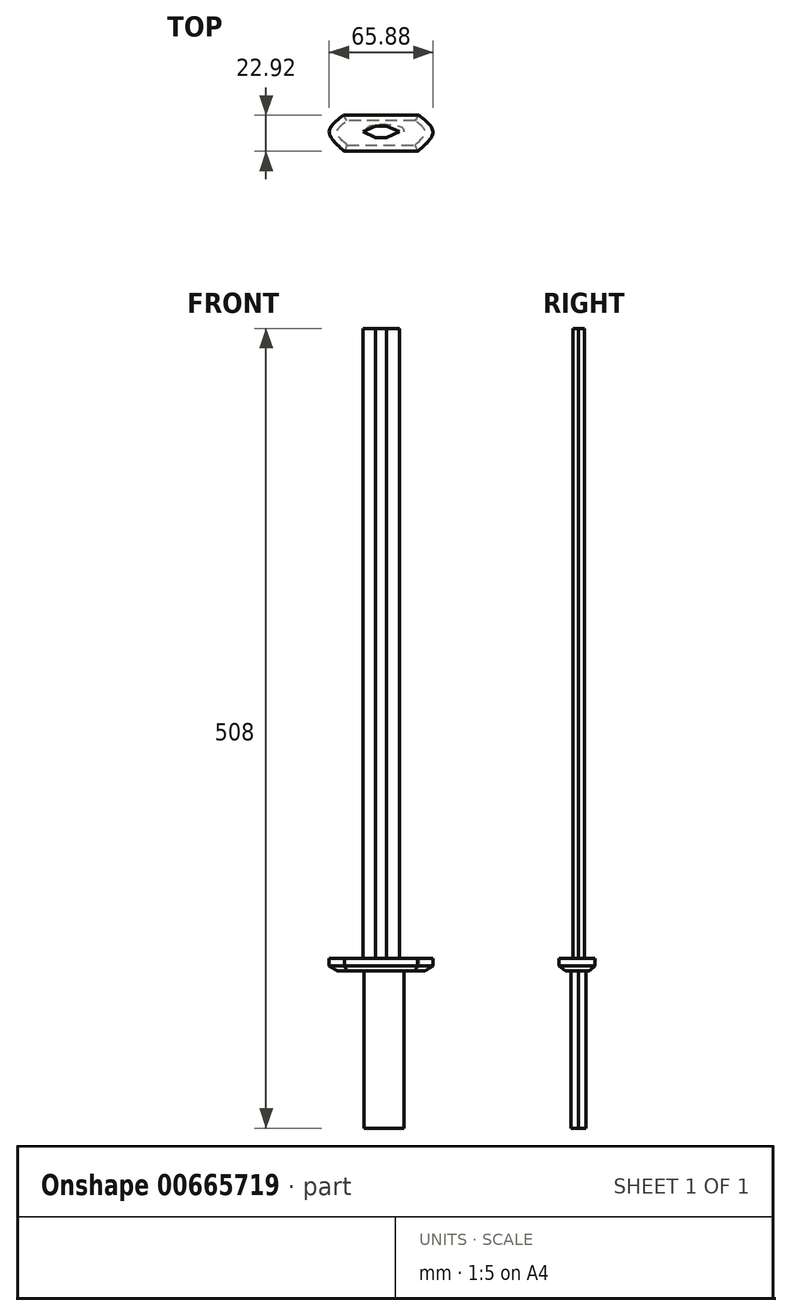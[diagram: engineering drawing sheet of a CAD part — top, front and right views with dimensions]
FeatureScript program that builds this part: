
annotation { "Feature Type Name" : "Feature", "Feature Type Description" : "" }
export const myFeature = defineFeature(function(context is Context, id is Id, definition is map)
    precondition{}
    {
        {
            var Q0;
            Q0=qCreatedBy(makeId("Top.planeOp"),FACE);
            var sketch = newSketch(context, id + "F0", { "sketchPlane" : qUnion([Q0])});
            skFitSpline(sketch, "E0", {"points": [v(-23.96, 10.4) * mm, v(-32.94, 0) * mm, v(-23.2, -12.5) * mm], "startDerivative": vector(-27.64, -20.96) * mm, "endDerivative": vector(28.5, -24.82) * mm});
            skFitSpline(sketch, "E1.MirrorCS", {"points": [v(23.96, 10.4) * mm, v(32.94, 0) * mm, v(23.2, -12.5) * mm], "startDerivative": vector(27.64, -20.96) * mm, "endDerivative": vector(-28.5, -24.82) * mm});
            skLineSegment(sketch, "E2", {"start": v(-23.96, 10.4) * mm, "end": v(23.96, 10.4) * mm});
            skLineSegment(sketch, "E3", {"start": v(-23.2, -12.5) * mm, "end": v(23.2, -12.5) * mm});
            skSolve(sketch);
        }
        {
            var Q0;
            Q0 = qSketchRegion(id + "F0", true);
            extrude(context, id + "F1", {"entities" : qUnion([Q0]), "depth" : 5 * mm, "offsetDistance" : 25 * mm});
        }
        {
            var Q0;
            Q0=makeQuery(id+"F1.opExtrude","CAP_FACE",FACE,{"disambiguationData":[OSD([sQuery(id+"F0.wireOp",EDGE,"E0"),sQuery(id+"F0.wireOp",EDGE,"E1.MirrorCS"),sQuery(id+"F0.wireOp",EDGE,"E2"),sQuery(id+"F0.wireOp",EDGE,"E3")])],"isStart":false});
            var sketch = newSketch(context, id + "F2", { "sketchPlane" : qUnion([Q0])});
            skLineSegment(sketch, "E4", {"start": v(-11.56, 0) * mm, "end": v(-3.48, 3.66) * mm});
            skLineSegment(sketch, "E5.MirrorCS", {"start": v(-11.56, 0) * mm, "end": v(-3.48, -3.66) * mm});
            skPoint(sketch, "E6.2.internal.orphan", {"position": v(15.88, 0) * mm});
            skLineSegment(sketch, "E7", {"start": v(-3.48, -3.66) * mm, "end": v(0, -3.66) * mm});
            skLineSegment(sketch, "E8", {"start": v(-3.48, 3.66) * mm, "end": v(0, 3.66) * mm});
            skLineSegment(sketch, "E9.MirrorCS", {"start": v(11.56, 0) * mm, "end": v(3.48, -3.66) * mm});
            skLineSegment(sketch, "E10.MirrorCS", {"start": v(11.56, 0) * mm, "end": v(3.48, 3.66) * mm});
            skLineSegment(sketch, "E11.MirrorCS", {"start": v(3.48, 3.66) * mm, "end": v(0, 3.66) * mm});
            skLineSegment(sketch, "E12.MirrorCS", {"start": v(3.48, -3.66) * mm, "end": v(0, -3.66) * mm});
            skSolve(sketch);
        }
        {
            var Q0;
            Q0 = qSketchRegion(id + "F2", true);
            extrude(context, id + "F3", {"entities" : qUnion([Q0]), "operationType" : NewBodyOperationType.ADD, "depth" : 400 * mm, "offsetDistance" : 25 * mm});
        }
        {
            var Q0;
            Q0=makeQuery(id+"F1.opExtrude","CAP_FACE",FACE,{"disambiguationData":[OSD([sQuery(id+"F0.wireOp",EDGE,"E0"),sQuery(id+"F0.wireOp",EDGE,"E1.MirrorCS"),sQuery(id+"F0.wireOp",EDGE,"E2"),sQuery(id+"F0.wireOp",EDGE,"E3")])],"isStart":true});
            cPlane(context, id + "F4", {"entities" : qUnion([Q0]), "cplaneType" : CPlaneType.OFFSET, "offset" : 3 * mm, "width" : 150 * mm, "height" : 150 * mm});
        }
        {
            var Q0;
            Q0=qCreatedBy(id+"F4.planeOp",FACE);
            var sketch = newSketch(context, id + "F5", { "sketchPlane" : qUnion([Q0])});
            skFitSpline(sketch, "E13", {"points": [v(-21.52, 8.47) * mm, v(-27.91, 0) * mm, v(-21.7, -6.94) * mm], "startDerivative": vector(-18.88, -16.94) * mm, "endDerivative": vector(18.92, -13.85) * mm});
            skLineSegment(sketch, "E14", {"start": v(-21.52, 8.47) * mm, "end": v(0, 8.47) * mm});
            skLineSegment(sketch, "E15", {"start": v(-21.7, -6.94) * mm, "end": v(0, -6.94) * mm});
            skLineSegment(sketch, "E16.MirrorCS", {"start": v(21.52, 8.47) * mm, "end": v(0, 8.47) * mm});
            skFitSpline(sketch, "E17.MirrorCS", {"points": [v(21.52, 8.47) * mm, v(27.91, 0) * mm, v(21.7, -6.94) * mm], "startDerivative": vector(18.88, -16.94) * mm, "endDerivative": vector(-18.92, -13.85) * mm});
            skLineSegment(sketch, "E18.MirrorCS", {"start": v(21.7, -6.94) * mm, "end": v(0, -6.94) * mm});
            skSolve(sketch);
        }
        {
            var Q1;
            Q1=makeQuery(id+"F5.imprint","IMPRINT",FACE,{"disambiguationData":[TD([[makeQuery(id+"F5.imprint","IMPRINT",EDGE,{"derivedFrom":sQuery(id+"F5.wireOp",EDGE,"E13")}),1.0]])]});
            var Q2;
            Q2=makeQuery(id+"F1.opExtrude","CAP_FACE",FACE,{"disambiguationData":[OSD([sQuery(id+"F0.wireOp",EDGE,"E0"),sQuery(id+"F0.wireOp",EDGE,"E1.MirrorCS"),sQuery(id+"F0.wireOp",EDGE,"E2"),sQuery(id+"F0.wireOp",EDGE,"E3")])],"isStart":true});
            loft(context, id + "F6", {"operationType" : NewBodyOperationType.ADD, "sheetProfilesArray" : [{ "sheetProfileEntities" : qUnion([Q1]) }, { "sheetProfileEntities" : qUnion([Q2]) }]});
        }
        {
            var Q0;
            Q0=makeQuery(id+"F6.opLoft","CAP_FACE",FACE,{"disambiguationData":[OSD([makeQuery(id+"F5.imprint","IMPRINT",FACE,{"disambiguationData":[TD([[makeQuery(id+"F5.imprint","IMPRINT",EDGE,{"derivedFrom":sQuery(id+"F5.wireOp",EDGE,"E13")}),1.0]])]})])],"isStart":true});
            var sketch = newSketch(context, id + "F7", { "sketchPlane" : qUnion([Q0])});
            skFitSpline(sketch, "E19", {"points": [v(-10.98, 0) * mm, v(-6.37, 3.9) * mm, v(12.14, 3.28) * mm, v(14.57, 0) * mm], "startDerivative": vector(10.87, 15.93) * mm, "endDerivative": vector(5.1, -22.05) * mm});
            skFitSpline(sketch, "E20.MirrorCS", {"points": [v(-10.98, 0) * mm, v(-6.37, -3.9) * mm, v(12.14, -3.28) * mm, v(14.57, 0) * mm], "startDerivative": vector(10.87, -15.93) * mm, "endDerivative": vector(5.1, 22.05) * mm});
            skSolve(sketch);
        }
        {
            var Q0;
            Q0=makeQuery(id+"F7.imprint","IMPRINT",FACE,{"disambiguationData":[TD([[makeQuery(id+"F7.imprint","IMPRINT",EDGE,{"derivedFrom":sQuery(id+"F7.wireOp",EDGE,"E19")}),-1.0]])]});
            extrude(context, id + "F8", {"entities" : qUnion([Q0]), "operationType" : NewBodyOperationType.ADD, "depth" : 100 * mm, "offsetDistance" : 25 * mm});
        }
    });
